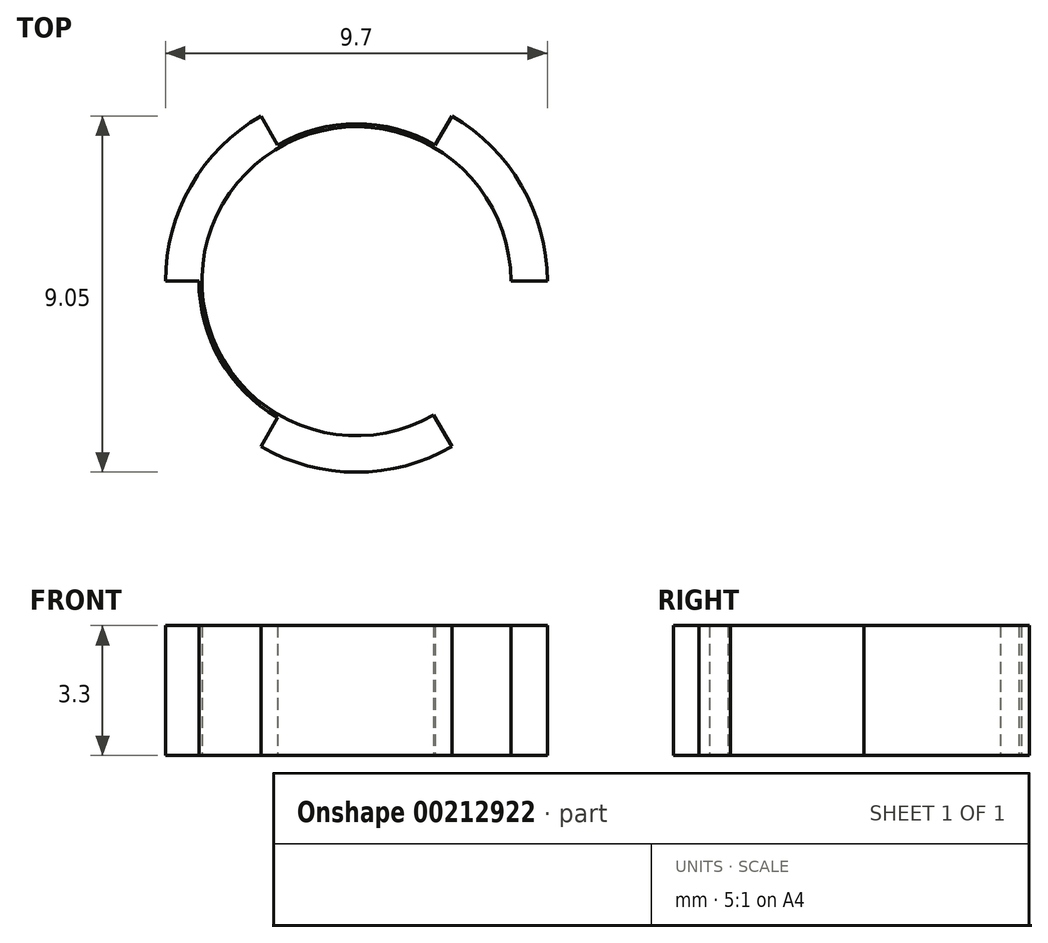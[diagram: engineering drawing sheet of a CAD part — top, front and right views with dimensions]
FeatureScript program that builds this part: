
annotation { "Feature Type Name" : "Feature", "Feature Type Description" : "" }
export const myFeature = defineFeature(function(context is Context, id is Id, definition is map)
    precondition{}
    {
        {
            var Q0;
            Q0=qCreatedBy(makeId("Top.planeOp"),FACE);
            var sketch = newSketch(context, id + "F0", { "sketchPlane" : qUnion([Q0])});
            skCircle(sketch, "E0", {"center": v(0, 0) * mm, "radius": 3.92 * mm});
            skCircle(sketch, "E1", {"center": v(0, 0) * mm, "radius": 4 * mm});
            skCircle(sketch, "E2", {"center": v(0, 0) * mm, "radius": 4.85 * mm});
            skLineSegment(sketch, "E3", {"start": v(-4.85, 0) * mm, "end": v(4.85, 0) * mm});
            skLineSegment(sketch, "E4", {"start": v(-2.43, -4.2) * mm, "end": v(2.43, 4.2) * mm});
            skLineSegment(sketch, "E5", {"start": v(2.43, -4.2) * mm, "end": v(-2.43, 4.2) * mm});
            skSolve(sketch);
        }
        {
            var Q0;
            {var subQ0=sQuery(id+"F0.wireOp",EDGE,"E4");var subQ1=sQuery(id+"F0.wireOp",EDGE,"E1");var subQ2=makeQuery(id+"F0.imprint","INTERSECT",VERTEX,{"disambiguationData":[OD(0.0)],"derivedFrom":[subQ1,subQ0]});Q0=makeQuery(id+"F0.imprint","IMPRINT",FACE,{"disambiguationData":[TD([[makeQuery(id+"F0.imprint","IMPRINT",EDGE,{"disambiguationData":[TD([[subQ2,1.0]])],"derivedFrom":subQ1}),-1.0]])]});}
            var Q1;
            {var subQ0=sQuery(id+"F0.wireOp",EDGE,"E4");var subQ1=sQuery(id+"F0.wireOp",EDGE,"E0");var subQ2=makeQuery(id+"F0.imprint","INTERSECT",VERTEX,{"disambiguationData":[OD(0.0)],"derivedFrom":[subQ1,subQ0]});Q1=makeQuery(id+"F0.imprint","IMPRINT",FACE,{"disambiguationData":[TD([[makeQuery(id+"F0.imprint","IMPRINT",EDGE,{"disambiguationData":[TD([[subQ2,1.0]])],"derivedFrom":subQ1}),-1.0]])]});}
            var Q2;
            {var subQ0=sQuery(id+"F0.wireOp",EDGE,"E4");var subQ1=sQuery(id+"F0.wireOp",EDGE,"E0");var subQ2=makeQuery(id+"F0.imprint","INTERSECT",VERTEX,{"disambiguationData":[OD(0.0)],"derivedFrom":[subQ1,subQ0]});Q2=makeQuery(id+"F0.imprint","IMPRINT",FACE,{"disambiguationData":[TD([[makeQuery(id+"F0.imprint","IMPRINT",EDGE,{"disambiguationData":[TD([[subQ2,-1.0]])],"derivedFrom":subQ1}),-1.0]])]});}
            var Q3;
            {var subQ0=sQuery(id+"F0.wireOp",EDGE,"E5");var subQ1=sQuery(id+"F0.wireOp",EDGE,"E0");var subQ2=makeQuery(id+"F0.imprint","INTERSECT",VERTEX,{"disambiguationData":[OD(0.0)],"derivedFrom":[subQ1,subQ0]});Q3=makeQuery(id+"F0.imprint","IMPRINT",FACE,{"disambiguationData":[TD([[makeQuery(id+"F0.imprint","IMPRINT",EDGE,{"disambiguationData":[TD([[subQ2,-1.0]])],"derivedFrom":subQ1}),-1.0]])]});}
            var Q4;
            {var subQ0=sQuery(id+"F0.wireOp",EDGE,"E5");var subQ1=sQuery(id+"F0.wireOp",EDGE,"E1");var subQ2=makeQuery(id+"F0.imprint","INTERSECT",VERTEX,{"disambiguationData":[OD(0.0)],"derivedFrom":[subQ1,subQ0]});Q4=makeQuery(id+"F0.imprint","IMPRINT",FACE,{"disambiguationData":[TD([[makeQuery(id+"F0.imprint","IMPRINT",EDGE,{"disambiguationData":[TD([[subQ2,-1.0]])],"derivedFrom":subQ1}),-1.0]])]});}
            var Q5;
            {var subQ0=sQuery(id+"F0.wireOp",EDGE,"E3");var subQ1=sQuery(id+"F0.wireOp",EDGE,"E0");var subQ2=makeQuery(id+"F0.imprint","INTERSECT",VERTEX,{"disambiguationData":[OD(1.0)],"derivedFrom":[subQ1,subQ0]});Q5=makeQuery(id+"F0.imprint","IMPRINT",FACE,{"disambiguationData":[TD([[makeQuery(id+"F0.imprint","IMPRINT",EDGE,{"disambiguationData":[TD([[subQ2,-1.0]])],"derivedFrom":subQ1}),-1.0]])]});}
            var Q6;
            {var subQ0=sQuery(id+"F0.wireOp",EDGE,"E4");var subQ1=sQuery(id+"F0.wireOp",EDGE,"E1");var subQ2=makeQuery(id+"F0.imprint","INTERSECT",VERTEX,{"disambiguationData":[OD(1.0)],"derivedFrom":[subQ1,subQ0]});Q6=makeQuery(id+"F0.imprint","IMPRINT",FACE,{"disambiguationData":[TD([[makeQuery(id+"F0.imprint","IMPRINT",EDGE,{"disambiguationData":[TD([[subQ2,-1.0]])],"derivedFrom":subQ1}),-1.0]])]});}
            var Q7;
            {var subQ0=sQuery(id+"F0.wireOp",EDGE,"E4");var subQ1=sQuery(id+"F0.wireOp",EDGE,"E0");var subQ2=makeQuery(id+"F0.imprint","INTERSECT",VERTEX,{"disambiguationData":[OD(1.0)],"derivedFrom":[subQ1,subQ0]});Q7=makeQuery(id+"F0.imprint","IMPRINT",FACE,{"disambiguationData":[TD([[makeQuery(id+"F0.imprint","IMPRINT",EDGE,{"disambiguationData":[TD([[subQ2,-1.0]])],"derivedFrom":subQ1}),-1.0]])]});}
            var Q8;
            {var subQ0=sQuery(id+"F0.wireOp",EDGE,"E3");var subQ1=sQuery(id+"F0.wireOp",EDGE,"E0");var subQ2=makeQuery(id+"F0.imprint","INTERSECT",VERTEX,{"disambiguationData":[OD(0.0)],"derivedFrom":[subQ1,subQ0]});Q8=makeQuery(id+"F0.imprint","IMPRINT",FACE,{"disambiguationData":[TD([[makeQuery(id+"F0.imprint","IMPRINT",EDGE,{"disambiguationData":[TD([[subQ2,1.0]])],"derivedFrom":subQ1}),-1.0]])]});}
            extrude(context, id + "F1", {"entities" : qUnion([Q0, Q1, Q2, Q3, Q4, Q5, Q6, Q7, Q8]), "depth" : 3.3 * mm});
        }
    });
